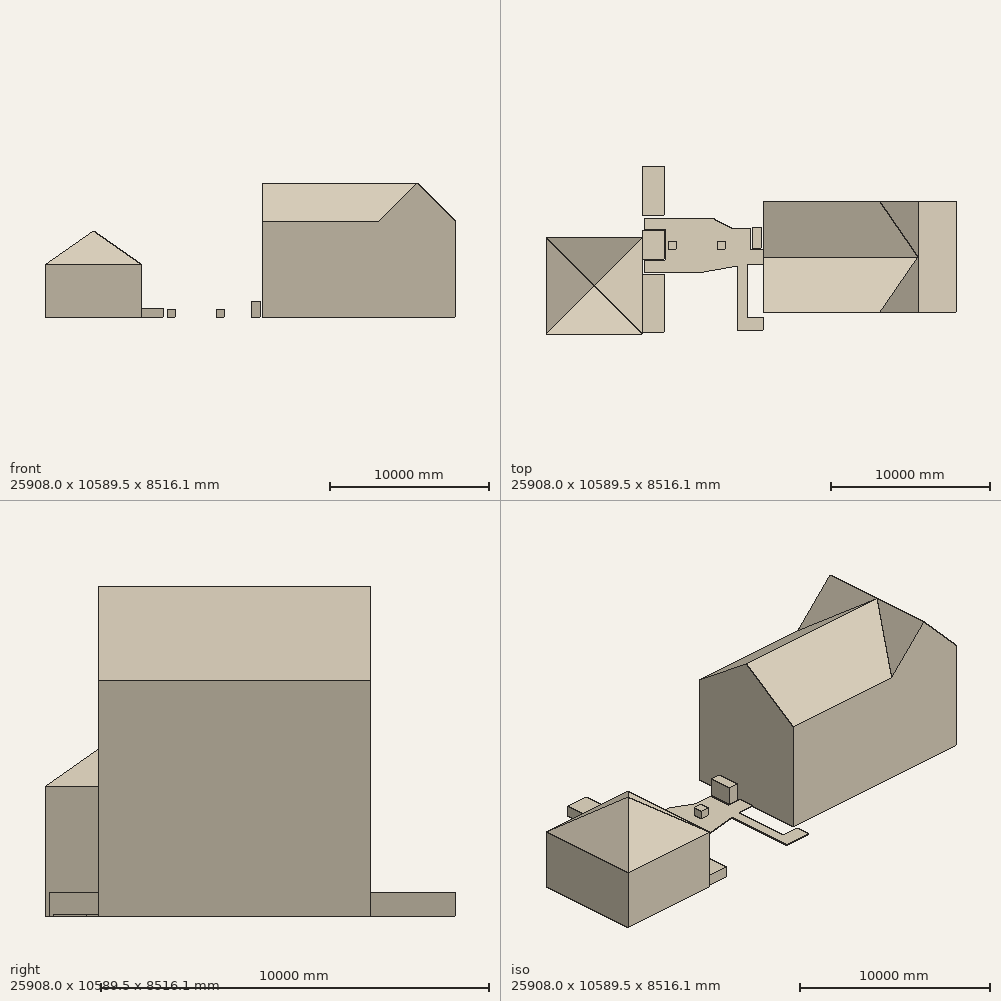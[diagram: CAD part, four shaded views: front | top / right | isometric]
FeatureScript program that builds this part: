
annotation { "Feature Type Name" : "Feature", "Feature Type Description" : "" }
export const myFeature = defineFeature(function(context is Context, id is Id, definition is map)
    precondition{}
    {
        {
            var Q0;
            Q0=qCreatedBy(makeId("Top.planeOp"),FACE);
            var sketch = newSketch(context, id + "F0", { "sketchPlane" : qUnion([Q0])});
            skLineSegment(sketch, "E0.bottom", {"start": v(0, 1371.6) * mm, "end": v(12192, 1371.6) * mm});
            skLineSegment(sketch, "E0.top", {"start": v(0, 8382) * mm, "end": v(12192, 8382) * mm});
            skLineSegment(sketch, "E0.left", {"start": v(0, 1371.6) * mm, "end": v(0, 8382) * mm});
            skLineSegment(sketch, "E0.right", {"start": v(12192, 1371.6) * mm, "end": v(12192, 8382) * mm});
            skLineSegment(sketch, "E1", {"start": v(0, 0) * mm, "end": v(12192, 0) * mm});
            skLineSegment(sketch, "E2", {"start": v(0, 0) * mm, "end": v(-7620, 0) * mm});
            skLineSegment(sketch, "E3.bottom", {"start": v(-7620, 6096) * mm, "end": v(-13716, 6096) * mm});
            skLineSegment(sketch, "E3.top", {"start": v(-7620, 0) * mm, "end": v(-13716, 0) * mm});
            skLineSegment(sketch, "E3.left", {"start": v(-7620, 6096) * mm, "end": v(-7620, 0) * mm});
            skLineSegment(sketch, "E3.right", {"start": v(-13716, 6096) * mm, "end": v(-13716, 0) * mm});
            skLineSegment(sketch, "E4", {"start": v(12192, 10589.46) * mm, "end": v(-7620, 10589.46) * mm});
            skLineSegment(sketch, "E5", {"start": v(-7620, 10589.46) * mm, "end": v(-7620, 7476.08) * mm});
            skLineSegment(sketch, "E6.bottom", {"start": v(-7620, 7476.08) * mm, "end": v(-6248.4, 7476.08) * mm});
            skLineSegment(sketch, "E6.top", {"start": v(-7620, 10589.46) * mm, "end": v(-6248.4, 10589.46) * mm});
            skLineSegment(sketch, "E6.left", {"start": v(-7620, 7476.08) * mm, "end": v(-7620, 10589.46) * mm});
            skLineSegment(sketch, "E6.right", {"start": v(-6248.4, 7476.08) * mm, "end": v(-6248.4, 10589.46) * mm});
            skLineSegment(sketch, "E7.bottom", {"start": v(-7620, 6561.68) * mm, "end": v(-6248.4, 6561.68) * mm});
            skLineSegment(sketch, "E7.top", {"start": v(-7620, 4746.48) * mm, "end": v(-6248.4, 4746.48) * mm});
            skLineSegment(sketch, "E7.left", {"start": v(-7620, 6561.68) * mm, "end": v(-7620, 4746.48) * mm});
            skLineSegment(sketch, "E7.right", {"start": v(-6248.4, 6561.68) * mm, "end": v(-6248.4, 4746.48) * mm});
            skLineSegment(sketch, "E8.bottom", {"start": v(-7620, 3797.46) * mm, "end": v(-6248.4, 3797.46) * mm});
            skLineSegment(sketch, "E8.top", {"start": v(-7620, 112.54) * mm, "end": v(-6248.4, 112.54) * mm});
            skLineSegment(sketch, "E8.left", {"start": v(-7620, 3797.46) * mm, "end": v(-7620, 112.54) * mm});
            skLineSegment(sketch, "E8.right", {"start": v(-6248.4, 3797.46) * mm, "end": v(-6248.4, 112.54) * mm});
            skLineSegment(sketch, "E9", {"start": v(12192, 0) * mm, "end": v(12192, 1371.6) * mm});
            skLineSegment(sketch, "E10", {"start": v(12192, 10589.46) * mm, "end": v(12192, 8382) * mm});
            skLineSegment(sketch, "E11", {"start": v(-7620, 6096) * mm, "end": v(-7620, 6774.4) * mm});
            skSolve(sketch);
        }
        {
            var Q0;
            Q0=makeQuery(id+"F0.imprint","IMPRINT",FACE,{"disambiguationData":[TD([[makeQuery(id+"F0.imprint","IMPRINT",EDGE,{"derivedFrom":sQuery(id+"F0.wireOp",EDGE,"E8.bottom")}),-1.0]])]});
            var Q1;
            Q1=makeQuery(id+"F0.imprint","IMPRINT",FACE,{"disambiguationData":[TD([[makeQuery(id+"F0.imprint","IMPRINT",EDGE,{"derivedFrom":sQuery(id+"F0.wireOp",EDGE,"E7.bottom")}),-1.0]])]});
            var Q2;
            Q2=makeQuery(id+"F0.imprint","IMPRINT",FACE,{"disambiguationData":[TD([[makeQuery(id+"F0.imprint","IMPRINT",EDGE,{"derivedFrom":sQuery(id+"F0.wireOp",EDGE,"E6.bottom")}),1.0]])]});
            var Q3;
            Q3=sQuery(id+"F0.wireOp",EDGE,"E2");
            extrude(context, id + "F1", {"entities" : qUnion([Q0, Q1, Q2]), "surfaceEntities" : qUnion([Q3]), "depth" : 609.6 * mm, "offsetDistance" : 25.4 * mm});
        }
        {
            var Q0;
            Q0=makeQuery(id+"F0.imprint","IMPRINT",FACE,{"disambiguationData":[TD([[makeQuery(id+"F0.imprint","IMPRINT",EDGE,{"derivedFrom":sQuery(id+"F0.wireOp",EDGE,"E3.bottom")}),1.0]])]});
            extrude(context, id + "F2", {"entities" : qUnion([Q0]), "depth" : 5486.4 * mm, "offsetDistance" : 25.4 * mm});
        }
        {
            var Q0;
            Q0=makeQuery(id+"F2.opExtrude","CAP_FACE",FACE,{"disambiguationData":[OSD([sQuery(id+"F0.wireOp",EDGE,"E3.bottom"),sQuery(id+"F0.wireOp",EDGE,"E3.top"),sQuery(id+"F0.wireOp",EDGE,"E3.left"),sQuery(id+"F0.wireOp",EDGE,"E3.right")])],"isStart":false});
            chamfer(context, id + "F3", {"entities" : qUnion([Q0]), "chamferType" : ChamferType.OFFSET_ANGLE, "width" : 3048 * mm, "oppositeDirection" : false, "angle" : 35 * degree, "tangentPropagation" : true});
        }
        {
            var Q0;
            Q0=makeQuery(id+"F0.imprint","IMPRINT",FACE,{"disambiguationData":[TD([[makeQuery(id+"F0.imprint","IMPRINT",EDGE,{"derivedFrom":sQuery(id+"F0.wireOp",EDGE,"E0.bottom")}),1.0]])]});
            extrude(context, id + "F4", {"entities" : qUnion([Q0]), "depth" : 6096 * mm, "offsetDistance" : 25.4 * mm});
        }
        {
            var Q0;
            Q0=makeQuery(id+"F4.opExtrude","SWEPT_FACE",FACE,{"disambiguationData":[OSD([sQuery(id+"F0.wireOp",EDGE,"E0.bottom")])]});
            var sketch = newSketch(context, id + "F5", { "sketchPlane" : qUnion([Q0])});
            skLineSegment(sketch, "E12", {"start": v(12192, 6096) * mm, "end": v(9771.91, 8516.09) * mm});
            skLineSegment(sketch, "E13", {"start": v(9771.91, 8516.09) * mm, "end": v(7351.82, 6096) * mm});
            skSolve(sketch);
        }
        {
            var Q0;
            {var subQ0=sQuery(id+"F5.wireOp",EDGE,"E12");Q0=makeQuery(id+"F5.imprint","IMPRINT",FACE,{"disambiguationData":[TD([[makeQuery(id+"F5.imprint","IMPRINT",EDGE,{"derivedFrom":subQ0}),1.0]])]});}
            var Q1;
            Q1=makeQuery(id+"F4.opExtrude","CAP_VERTEX",VERTEX,{"disambiguationData":[OSD([sQuery(id+"F0.wireOp",EDGE,"E0.top"),sQuery(id+"F0.wireOp",EDGE,"E0.right")])],"isStart":false});
            extrude(context, id + "F6", {"entities" : qUnion([Q0]), "operationType" : NewBodyOperationType.ADD, "endBound" : BoundingType.UP_TO_VERTEX, "oppositeDirection" : true, "depth" : 25.4 * mm, "endBoundEntityVertex" : qUnion([Q1]), "offsetDistance" : 25.4 * mm});
        }
        {
            var Q0;
            Q0=makeQuery(id+"F4.opExtrude","SWEPT_FACE",FACE,{"disambiguationData":[OSD([sQuery(id+"F0.wireOp",EDGE,"E0.left")])]});
            var sketch = newSketch(context, id + "F7", { "sketchPlane" : qUnion([Q0])});
            skLineSegment(sketch, "E14", {"start": v(-8382, 6096) * mm, "end": v(-4876.8, 8509.57) * mm});
            skLineSegment(sketch, "E15", {"start": v(-4876.8, 8509.57) * mm, "end": v(-1371.6, 6096) * mm});
            skSolve(sketch);
        }
        {
            var Q0;
            Q0=makeQuery(id+"F7.imprint","IMPRINT",FACE,{"disambiguationData":[TD([[makeQuery(id+"F7.imprint","IMPRINT",EDGE,{"derivedFrom":sQuery(id+"F7.wireOp",EDGE,"E14")}),-1.0]])]});
            var Q1;
            Q1=makeQuery(id+"F6.opExtrude","SWEPT_FACE",FACE,{"disambiguationData":[OSD([sQuery(id+"F5.wireOp",EDGE,"E13")])]});
            extrude(context, id + "F8", {"entities" : qUnion([Q0]), "operationType" : NewBodyOperationType.ADD, "endBound" : BoundingType.UP_TO_SURFACE, "oppositeDirection" : true, "depth" : 25.4 * mm, "endBoundEntityFace" : qUnion([Q1]), "offsetDistance" : 25.4 * mm});
        }
        {
            var Q0;
            Q0 = qSketchRegion(id + "F0", true);
            var Q1;
            Q1=sQuery(id+"F0.wireOp",EDGE,"E2");
            var Q2;
            Q2=sQuery(id+"F0.wireOp",EDGE,"E1");
            var Q3;
            Q3=sQuery(id+"F0.wireOp",EDGE,"E10");
            var Q4;
            Q4=sQuery(id+"F0.wireOp",EDGE,"E4");
            var Q5;
            Q5=sQuery(id+"F0.wireOp",EDGE,"E5");
            var Q6;
            Q6=sQuery(id+"F0.wireOp",EDGE,"E9");
            var Q7;
            Q7=sQuery(id+"F0.wireOp",EDGE,"E11");
            extrude(context, id + "F9", {"entities" : qUnion([Q0]), "bodyType" : ToolBodyType.SURFACE, "surfaceEntities" : qUnion([Q1, Q2, Q3, Q4, Q5, Q6, Q7]), "depth" : 2133.6 * mm, "offsetDistance" : 25.4 * mm});
        }
        {
            var Q0;
            Q0=qCreatedBy(makeId("Top.planeOp"),FACE);
            var sketch = newSketch(context, id + "F10", { "sketchPlane" : qUnion([Q0])});
            skLineSegment(sketch, "E16.bottom", {"start": v(-5475.3, 6005.4) * mm, "end": v(-2884.5, 6005.4) * mm});
            skLineSegment(sketch, "E16.top", {"start": v(-5475.3, 5218) * mm, "end": v(-2884.5, 5218) * mm});
            skLineSegment(sketch, "E16.left", {"start": v(-5475.3, 6005.4) * mm, "end": v(-5475.3, 5218) * mm});
            skLineSegment(sketch, "E16.right", {"start": v(-2884.5, 6005.4) * mm, "end": v(-2884.5, 5218) * mm});
            skLineSegment(sketch, "E17.bottom", {"start": v(-5348.3, 6005.4) * mm, "end": v(-3011.5, 6005.4) * mm});
            skLineSegment(sketch, "E17.top", {"start": v(-5348.3, 6513.4) * mm, "end": v(-3011.5, 6513.4) * mm});
            skLineSegment(sketch, "E17.left", {"start": v(-5348.3, 6005.4) * mm, "end": v(-5348.3, 6513.4) * mm});
            skLineSegment(sketch, "E17.right", {"start": v(-3011.5, 6005.4) * mm, "end": v(-3011.5, 6513.4) * mm});
            skLineSegment(sketch, "E18.bottom", {"start": v(-5475.3, 5878.4) * mm, "end": v(-5983.3, 5878.4) * mm});
            skLineSegment(sketch, "E18.top", {"start": v(-5475.3, 5345) * mm, "end": v(-5983.3, 5345) * mm});
            skLineSegment(sketch, "E18.left", {"start": v(-5475.3, 5878.4) * mm, "end": v(-5475.3, 5345) * mm});
            skLineSegment(sketch, "E18.right", {"start": v(-5983.3, 5878.4) * mm, "end": v(-5983.3, 5345) * mm});
            skLineSegment(sketch, "E19.bottom", {"start": v(-5348.3, 5218) * mm, "end": v(-3011.5, 5218) * mm});
            skLineSegment(sketch, "E19.top", {"start": v(-5348.3, 4710) * mm, "end": v(-3011.5, 4710) * mm});
            skLineSegment(sketch, "E19.left", {"start": v(-5348.3, 5218) * mm, "end": v(-5348.3, 4710) * mm});
            skLineSegment(sketch, "E19.right", {"start": v(-3011.5, 5218) * mm, "end": v(-3011.5, 4710) * mm});
            skLineSegment(sketch, "E20.bottom", {"start": v(-2884.5, 5878.4) * mm, "end": v(-2376.5, 5878.4) * mm});
            skLineSegment(sketch, "E20.top", {"start": v(-2884.5, 5345) * mm, "end": v(-2376.5, 5345) * mm});
            skLineSegment(sketch, "E20.left", {"start": v(-2884.5, 5878.4) * mm, "end": v(-2884.5, 5345) * mm});
            skLineSegment(sketch, "E20.right", {"start": v(-2376.5, 5878.4) * mm, "end": v(-2376.5, 5345) * mm});
            skLineSegment(sketch, "E21.bottom", {"start": v(-102.64, 6771.64) * mm, "end": v(-706.5, 6771.64) * mm});
            skLineSegment(sketch, "E21.top", {"start": v(-102.64, 5425.88) * mm, "end": v(-706.5, 5425.88) * mm});
            skLineSegment(sketch, "E21.left", {"start": v(-102.64, 6771.64) * mm, "end": v(-102.64, 5425.88) * mm});
            skLineSegment(sketch, "E21.right", {"start": v(-706.5, 6771.64) * mm, "end": v(-706.5, 5425.88) * mm});
            skSolve(sketch);
        }
        {
            var Q0;
            Q0=makeQuery(id+"F10.imprint","IMPRINT",FACE,{"disambiguationData":[TD([[makeQuery(id+"F10.imprint","IMPRINT",EDGE,{"derivedFrom":sQuery(id+"F10.wireOp",EDGE,"E17.bottom")}),1.0]])]});
            var Q1;
            Q1=makeQuery(id+"F10.imprint","IMPRINT",FACE,{"disambiguationData":[TD([[makeQuery(id+"F10.imprint","IMPRINT",EDGE,{"derivedFrom":sQuery(id+"F10.wireOp",EDGE,"E18.bottom")}),1.0]])]});
            var Q2;
            Q2=makeQuery(id+"F10.imprint","IMPRINT",FACE,{"disambiguationData":[TD([[makeQuery(id+"F10.imprint","IMPRINT",EDGE,{"derivedFrom":sQuery(id+"F10.wireOp",EDGE,"E19.bottom")}),-1.0]])]});
            var Q3;
            Q3=makeQuery(id+"F10.imprint","IMPRINT",FACE,{"disambiguationData":[TD([[makeQuery(id+"F10.imprint","IMPRINT",EDGE,{"derivedFrom":sQuery(id+"F10.wireOp",EDGE,"E20.bottom")}),-1.0]])]});
            extrude(context, id + "F11", {"entities" : qUnion([Q0, Q1, Q2, Q3]), "depth" : 508 * mm, "offsetDistance" : 25.4 * mm});
        }
        {
            var Q0;
            Q0=makeQuery(id+"F10.imprint","IMPRINT",FACE,{"disambiguationData":[TD([[makeQuery(id+"F10.imprint","IMPRINT",EDGE,{"derivedFrom":sQuery(id+"F10.wireOp",EDGE,"E21.bottom")}),1.0]])]});
            var Q1;
            {var subQ0=sQuery(id+"F10.wireOp",EDGE,"E17.bottom");Q1=makeQuery(id+"F10.imprint","IMPRINT",FACE,{"disambiguationData":[TD([[makeQuery(id+"F10.imprint","IMPRINT",EDGE,{"derivedFrom":subQ0}),-1.0]])]});}
            extrude(context, id + "F12", {"entities" : qUnion([Q0, Q1]), "depth" : 1016 * mm, "offsetDistance" : 25.4 * mm});
        }
        {
            var Q0;
            Q0=qCreatedBy(makeId("Top.planeOp"),FACE);
            var sketch = newSketch(context, id + "F13", { "sketchPlane" : qUnion([Q0])});
            skLineSegment(sketch, "E22", {"start": v(0, 5334) * mm, "end": v(-830.44, 5334) * mm});
            skLineSegment(sketch, "E23", {"start": v(-830.44, 5334) * mm, "end": v(-830.44, 6693.8) * mm});
            skLineSegment(sketch, "E24", {"start": v(-7525.4, 4649.55) * mm, "end": v(-7525.4, 3889.75) * mm});
            skLineSegment(sketch, "E25", {"start": v(-7525.4, 3889.75) * mm, "end": v(-4019.53, 3889.75) * mm});
            skLineSegment(sketch, "E26", {"start": v(0, 4419.6) * mm, "end": v(-1014.61, 4419.6) * mm});
            skLineSegment(sketch, "E27", {"start": v(-1014.61, 4419.6) * mm, "end": v(-1014.61, 1068.17) * mm});
            skLineSegment(sketch, "E28", {"start": v(-1014.61, 1068.17) * mm, "end": v(0, 1068.17) * mm});
            skLineSegment(sketch, "E29", {"start": v(0, 210.43) * mm, "end": v(-1624.21, 210.43) * mm});
            skLineSegment(sketch, "E30", {"start": v(-1624.21, 210.43) * mm, "end": v(-1624.21, 3889.75) * mm});
            skLineSegment(sketch, "E31", {"start": v(-7525.4, 7337.14) * mm, "end": v(-7525.4, 6612.83) * mm});
            skLineSegment(sketch, "E32", {"start": v(-7525.4, 6612.83) * mm, "end": v(-6208.95, 6612.83) * mm});
            skLineSegment(sketch, "E33", {"start": v(-6208.95, 6612.83) * mm, "end": v(-6208.95, 4649.55) * mm});
            skLineSegment(sketch, "E34", {"start": v(-6208.95, 4649.55) * mm, "end": v(-7525.4, 4649.55) * mm});
            skPoint(sketch, "E35.visualSharp", {"position": v(-830.44, 7274.43) * mm});
            skLineSegment(sketch, "E36", {"start": v(-7525.4, 7337.14) * mm, "end": v(-3237.66, 7344.6) * mm});
            skLineSegment(sketch, "E37", {"start": v(0, 210.43) * mm, "end": v(0, 1068.17) * mm});
            skLineSegment(sketch, "E38", {"start": v(0, 4419.6) * mm, "end": v(0, 5334) * mm});
            skLineSegment(sketch, "E39", {"start": v(-1624.21, 4312.11) * mm, "end": v(-4019.53, 3889.75) * mm});
            skLineSegment(sketch, "E40", {"start": v(-1624.21, 3889.75) * mm, "end": v(-1624.21, 4312.11) * mm});
            skLineSegment(sketch, "E41", {"start": v(-770.14, 6693.8) * mm, "end": v(-2003.85, 6691.66) * mm});
            skLineSegment(sketch, "E42", {"start": v(-2003.85, 6691.66) * mm, "end": v(-3237.66, 7344.6) * mm});
            skSolve(sketch);
        }
        {
            var Q0;
            Q0 = qSketchRegion(id + "F13", true);
            extrude(context, id + "F14", {"entities" : qUnion([Q0]), "depth" : 50.8 * mm, "offsetDistance" : 25.4 * mm});
        }
    });
